annotation { "Feature Type Name" : "Feature", "Feature Type Description" : "" }
export const myFeature = defineFeature(function(context is Context, id is Id, definition is map)
    precondition{}
    {
        {
            var Q0;
            Q0=qCreatedBy(makeId("Top.planeOp"),FACE);
            var sketch = newSketch(context, id + "F0", { "sketchPlane" : qUnion([Q0])});
            skLineSegment(sketch, "E0.bottom", {"start": v(50.8, -25.4) * mm, "end": v(-50.8, -25.4) * mm});
            skLineSegment(sketch, "E0.top", {"start": v(50.8, 25.4) * mm, "end": v(-50.8, 25.4) * mm});
            skLineSegment(sketch, "E0.left", {"start": v(50.8, -25.4) * mm, "end": v(50.8, 25.4) * mm});
            skLineSegment(sketch, "E0.right", {"start": v(-50.8, -25.4) * mm, "end": v(-50.8, 25.4) * mm});
            skPoint(sketch, "E0.middle", {"position": v(0, 0) * mm});
            skSolve(sketch);
        }
        {
            var Q0;
            Q0 = qSketchRegion(id + "F0", true);
            extrude(context, id + "F1", {"entities" : qUnion([Q0]), "depth" : 6.35 * mm, "offsetDistance" : 25.4 * mm});
        }
        {
            var Q0;
            Q0=makeQuery(id+"F1.opExtrude","CAP_FACE",FACE,{"disambiguationData":[OSD([sQuery(id+"F0.wireOp",EDGE,"E0.bottom"),sQuery(id+"F0.wireOp",EDGE,"E0.top"),sQuery(id+"F0.wireOp",EDGE,"E0.left"),sQuery(id+"F0.wireOp",EDGE,"E0.right")])],"isStart":false});
            var sketch = newSketch(context, id + "F2", { "sketchPlane" : qUnion([Q0])});
            skText(sketch, "E1", { "text": "Jason Komisar\n", "fontName": "Tinos-Regular.ttf"});
            const initialGuessF2  = {"E1": [-0.04357, 0.00958, 1, 0, 0.01042]};
            skSetInitialGuess(sketch, initialGuessF2);
            skSolve(sketch);
        }
        {
            var Q0;
            Q0=makeQuery(id+"F2.imprint","IMPRINT",FACE,{"disambiguationData":[TD([[makeQuery(id+"F2.imprint","IMPRINT",EDGE,{"derivedFrom":sQuery(id+"F2.wireOp",EDGE,"E1.sketch_text.stroke-0")}),1.0]])]});
            var sketch = newSketch(context, id + "F3", { "sketchPlane" : qUnion([Q0])});
            skSolve(sketch);
        }
        {
            var Q0;
            Q0 = qSketchRegion(id + "F2", true);
            extrude(context, id + "F4", {"entities" : qUnion([Q0]), "operationType" : NewBodyOperationType.REMOVE, "oppositeDirection" : true, "depth" : 3.17 * mm, "offsetDistance" : 25.4 * mm});
        }
        {
            var Q0;
            Q0=makeQuery(id+"F3.imprint","IMPRINT",FACE,{"disambiguationData":[TD([[makeQuery(id+"F3.imprint","IMPRINT",EDGE,{"derivedFrom":makeQuery(id+"F2.imprint","IMPRINT",EDGE,{"derivedFrom":sQuery(id+"F2.wireOp",EDGE,"E1.sketch_text.stroke-0")})}),1.0]])]});
            var sketch = newSketch(context, id + "F5", { "sketchPlane" : qUnion([Q0])});
            skSolve(sketch);
        }
        {
            var Q0;
            Q0=makeQuery(id+"F3.imprint","IMPRINT",FACE,{"disambiguationData":[TD([[makeQuery(id+"F3.imprint","IMPRINT",EDGE,{"derivedFrom":makeQuery(id+"F2.imprint","IMPRINT",EDGE,{"derivedFrom":sQuery(id+"F2.wireOp",EDGE,"E1.sketch_text.stroke-0")})}),1.0]])]});
            var sketch = newSketch(context, id + "F6", { "sketchPlane" : qUnion([Q0])});
            skCircle(sketch, "E2", {"center": v(-31.63, -11.33) * mm, "radius": 9.27 * mm});
            skSolve(sketch);
        }
        {
            var Q0;
            Q0 = qSketchRegion(id + "F6", true);
            extrude(context, id + "F7", {"entities" : qUnion([Q0]), "operationType" : NewBodyOperationType.ADD, "depth" : 3.17 * mm, "offsetDistance" : 25.4 * mm});
        }
        {
            var Q0;
            Q0=makeQuery(id+"F7.opExtrude","CAP_FACE",FACE,{"disambiguationData":[OSD([sQuery(id+"F6.wireOp",EDGE,"E2")])],"isStart":false});
            var sketch = newSketch(context, id + "F8", { "sketchPlane" : qUnion([Q0])});
            skFitSpline(sketch, "E3", {"points": [v(-30.79, -3.96) * mm, v(-32.98, -4.5) * mm, v(-34.87, -5.85) * mm, v(-34.49, -9.56) * mm, v(-33.58, -11.22) * mm, v(-35.55, -14.77) * mm, v(-36.45, -17.26) * mm, v(-32.37, -19.08) * mm, v(-28.9, -19.15) * mm, v(-26.33, -17.64) * mm, v(-29.58, -13.18) * mm, v(-28.82, -11.97) * mm, v(-27.91, -11.37) * mm, v(-28.37, -10.39) * mm, v(-27.46, -9.4) * mm, v(-28.44, -6.16) * mm, v(-28.14, -4.95) * mm, v(-30.79, -3.96) * mm]});
            skSolve(sketch);
        }
        {
            var Q0;
            Q0=makeQuery(id+"F8.imprint","IMPRINT",FACE,{"disambiguationData":[TD([[makeQuery(id+"F8.imprint","IMPRINT",EDGE,{"derivedFrom":sQuery(id+"F8.wireOp",EDGE,"E3")}),1.0]])]});
            extrude(context, id + "F9", {"entities" : qUnion([Q0]), "operationType" : NewBodyOperationType.REMOVE, "oppositeDirection" : true, "depth" : 1.27 * mm, "offsetDistance" : 25.4 * mm});
        }
        {
            var Q0;
            Q0=makeQuery(id+"F6.imprint","IMPRINT",FACE,{"disambiguationData":[TD([[makeQuery(id+"F6.imprint","IMPRINT",EDGE,{"derivedFrom":sQuery(id+"F6.wireOp",EDGE,"E2")}),-1.0]])]});
            var sketch = newSketch(context, id + "F10", { "sketchPlane" : qUnion([Q0])});
            skFitSpline(sketch, "E4", {"points": [v(-4.38, -10.98) * mm, v(-4.11, -11.04) * mm, v(-2.78, -9.92) * mm, v(-1.4, -9.72) * mm, v(-1.46, -12.5) * mm, v(-1.79, -13.7) * mm, v(-2.45, -15.56) * mm, v(-3.25, -16.88) * mm, v(-3.05, -17.68) * mm, v(-2.05, -17.55) * mm, v(-1.46, -16.62) * mm, v(-1.06, -15.5) * mm, v(-0.73, -14.16) * mm, v(-0.8, -12.57) * mm, v(-0.66, -10.65) * mm, v(-0.66, -9.85) * mm, v(2.2, -9.78) * mm, v(2, -11.77) * mm, v(2.13, -12.57) * mm, v(1.8, -14.03) * mm, v(1.8, -15.3) * mm, v(2.2, -16.88) * mm, v(3.19, -17.81) * mm, v(4.65, -17.61) * mm, v(5.44, -16.68) * mm, v(5.64, -15.76) * mm, v(5.64, -15.16) * mm, v(5.38, -15.1) * mm, v(5.11, -15.76) * mm, v(4.38, -16.15) * mm, v(3.45, -15.89) * mm, v(2.79, -14.36) * mm, v(2.99, -13.1) * mm, v(3.05, -11.64) * mm, v(3.05, -10.65) * mm, v(3.39, -9.85) * mm, v(5.9, -9.59) * mm, v(5.97, -8.26) * mm, v(-2.65, -8.32) * mm, v(-3.65, -9.59) * mm, v(-4.38, -10.98) * mm]});
            skSolve(sketch);
        }
        {
            var Q0;
            Q0 = qSketchRegion(id + "F10", true);
            extrude(context, id + "F11", {"entities" : qUnion([Q0]), "operationType" : NewBodyOperationType.ADD, "depth" : 3.17 * mm, "offsetDistance" : 25.4 * mm});
        }
        {
            var Q0;
            Q0=makeQuery(id+"F5.imprint","IMPRINT",FACE,{"disambiguationData":[TD([[makeQuery(id+"F5.imprint","IMPRINT",EDGE,{"derivedFrom":makeQuery(id+"F3.imprint","IMPRINT",EDGE,{"derivedFrom":makeQuery(id+"F2.imprint","IMPRINT",EDGE,{"derivedFrom":sQuery(id+"F2.wireOp",EDGE,"E1.sketch_text.stroke-0")})})}),1.0]])]});
            var sketch = newSketch(context, id + "F12", { "sketchPlane" : qUnion([Q0])});
            skFitSpline(sketch, "E5", {"points": [v(20.54, -17.9) * mm, v(20.98, -16.12) * mm, v(21.4, -15.02) * mm, v(22.04, -13.4) * mm, v(23.03, -11.43) * mm, v(23.5, -10.36) * mm, v(23.62, -9.54) * mm, v(23.58, -8.04) * mm, v(23.62, -6.3) * mm, v(23.97, -4.84) * mm, v(24.53, -3.42) * mm, v(24.84, -2.67) * mm, v(25.47, -2.04) * mm, v(25.99, -1.45) * mm, v(29.81, -1.37) * mm, v(36.48, -1.4) * mm, v(37.15, -2.71) * mm, v(37.94, -4.96) * mm, v(39, -6.26) * mm, v(39.72, -7.96) * mm, v(40.54, -10.2) * mm, v(41.25, -12.81) * mm, v(41.85, -15.22) * mm, v(39.48, -17.5) * mm, v(36.52, -18.65) * mm, v(36.09, -18.69) * mm, v(35.7, -19.28) * mm, v(34.7, -19.32) * mm, v(32.61, -19.28) * mm, v(29.1, -19.28) * mm, v(23.58, -19.28) * mm, v(21.76, -19) * mm, v(20.54, -17.9) * mm]});
            skFitSpline(sketch, "E6", {"points": [v(34.03, -7.35) * mm, v(31.37, -7.22) * mm, v(29.45, -8.28) * mm, v(29.31, -8.61) * mm, v(31.24, -9.67) * mm, v(33.36, -9.47) * mm, v(34.22, -9.67) * mm, v(34.42, -10.36) * mm, v(33.63, -10.36) * mm, v(32.57, -10.36) * mm, v(31.64, -10.36) * mm, v(31.04, -10.87) * mm, v(31.64, -13.06) * mm, v(32.37, -12.26) * mm, v(34.69, -11.53) * mm, v(35.15, -9.74) * mm, v(34.36, -8.48) * mm, v(34.03, -7.35) * mm]});
            skFitSpline(sketch, "E7", {"points": [v(35.82, -7.48) * mm, v(35.62, -8.94) * mm, v(37.54, -9.67) * mm, v(38.74, -8.88) * mm, v(38.34, -7.55) * mm, v(37.48, -7.02) * mm, v(35.82, -7.48) * mm]});
            skCircle(sketch, "E8", {"center": v(36.83, -8.48) * mm, "radius": 0.52 * mm});
            skCircle(sketch, "E9", {"center": v(31.94, -8.36) * mm, "radius": 0.5 * mm});
            skFitSpline(sketch, "E10", {"points": [v(35.83, -10.13) * mm, v(36.23, -10.17) * mm, v(36.45, -10.65) * mm, v(36.52, -11.04) * mm, v(38.36, -12.64) * mm, v(39.09, -10.8) * mm, v(38.5, -10.36) * mm, v(37, -10.36) * mm, v(36.27, -9.88) * mm, v(35.83, -10.13) * mm]});
            skFitSpline(sketch, "E11", {"points": [v(32.88, -14.3) * mm, v(32.72, -14.69) * mm, v(32.18, -14.41) * mm, v(32.32, -14.04) * mm, v(32.88, -13.76) * mm, v(33.96, -12.84) * mm, v(34.65, -11.75) * mm, v(36.3, -11.73) * mm, v(38.32, -13.9) * mm, v(38.06, -14.28) * mm, v(37.16, -13.39) * mm, v(37.08, -14.14) * mm, v(36.66, -14.14) * mm, v(36.27, -12.7) * mm, v(36.11, -12.68) * mm, v(36.19, -14) * mm, v(35.8, -14.06) * mm, v(35.28, -12.48) * mm, v(35.18, -13.96) * mm, v(34.9, -14.16) * mm, v(34.42, -12.84) * mm, v(34.42, -14.06) * mm, v(33.94, -14.31) * mm, v(33.76, -13.53) * mm, v(32.88, -14.3) * mm]});
            skFitSpline(sketch, "E12", {"points": [v(21.06, -16.97) * mm, v(23.87, -15.14) * mm, v(25.51, -14.95) * mm, v(26.64, -10.36) * mm, v(29.03, -6.65) * mm, v(29.64, -6.32) * mm, v(29.17, -4.96) * mm, v(33.54, -5.34) * mm, v(32.88, -2.52) * mm, v(32.32, -1.25) * mm, v(31.1, -1.32) * mm, v(32.88, -4.12) * mm, v(32.88, -4.59) * mm, v(29.81, -1.37) * mm, v(25.99, -1.45) * mm, v(23.5, -10.36) * mm, v(21.06, -16.97) * mm]});
            skFitSpline(sketch, "E13", {"points": [v(32.88, -15.66) * mm, v(35, -18.47) * mm, v(35.93, -17.49) * mm, v(39.73, -14.9) * mm, v(38.98, -13.4) * mm, v(38.98, -12.47) * mm, v(39.64, -11.44) * mm, v(38.97, -10.54) * mm, v(38.74, -8.4) * mm, v(38.74, -7.55) * mm, v(41.04, -15.33) * mm, v(36.09, -18.69) * mm, v(35.7, -19.28) * mm, v(34.7, -19.32) * mm, v(32.88, -19.28) * mm, v(29.1, -19.28) * mm, v(28.38, -19.28) * mm, v(29.1, -18.65) * mm, v(28.42, -17.9) * mm, v(28.66, -16.31) * mm, v(32.32, -15.22) * mm, v(33.87, -14.67) * mm, v(38.34, -14.72) * mm, v(36.09, -16.64) * mm, v(34.7, -17.4) * mm, v(34.7, -17.2) * mm, v(32.88, -15.66) * mm]});
            skFitSpline(sketch, "E14", {"points": [v(22.57, -17.05) * mm, v(21.76, -17.9) * mm, v(25.99, -18.69) * mm, v(26.64, -16.65) * mm, v(29.1, -15.22) * mm, v(30.86, -15.22) * mm, v(27.48, -14.3) * mm, v(26.64, -15.22) * mm, v(24.84, -16.25) * mm, v(22.57, -17.05) * mm]});
            skFitSpline(sketch, "E15", {"points": [v(33.96, -2.04) * mm, v(36.48, -2.67) * mm, v(37.16, -4.57) * mm, v(36.09, -5.17) * mm, v(35.7, -4.44) * mm, v(34.7, -5.5) * mm, v(33.96, -2.04) * mm]});
            skFitSpline(sketch, "E16", {"points": [v(31.37, -14.14) * mm, v(27.3, -11.44) * mm, v(27.2, -8.88) * mm, v(29.81, -11.44) * mm, v(29.81, -12) * mm, v(29.81, -13.06) * mm, v(31.37, -14.14) * mm]});
            skFitSpline(sketch, "E17", {"points": [v(36.09, -5.5) * mm, v(35.56, -5.5) * mm, v(35.43, -5.9) * mm, v(35.7, -6.48) * mm, v(35.7, -6.7) * mm, v(36.09, -6.53) * mm, v(36.09, -6.17) * mm, v(36.09, -5.5) * mm]});
            skFitSpline(sketch, "E18", {"points": [v(31.73, -5.34) * mm, v(34.08, -6.46) * mm, v(34.16, -5.75) * mm, v(31.73, -5.34) * mm]});
            skFitSpline(sketch, "E19", {"points": [v(34.7, -7.85) * mm, v(35.42, -7.92) * mm, v(35.51, -7.7) * mm, v(34.8, -7.66) * mm, v(34.7, -7.85) * mm]});
            skFitSpline(sketch, "E20", {"points": [v(34.5, -8.33) * mm, v(34.54, -8.52) * mm, v(35.32, -8.4) * mm, v(35.46, -8.26) * mm, v(34.5, -8.33) * mm]});
            skFitSpline(sketch, "E21", {"points": [v(35.38, -9) * mm, v(35.36, -8.84) * mm, v(34.87, -8.8) * mm, v(34.87, -8.95) * mm, v(35.05, -9.03) * mm, v(35.38, -9) * mm]});
            skFitSpline(sketch, "E22", {"points": [v(39.01, -14.48) * mm, v(38.82, -14.67) * mm, v(38.93, -14.99) * mm, v(38.82, -15.13) * mm, v(38.5, -14.65) * mm, v(38.64, -14.34) * mm, v(39.01, -14.48) * mm]});
            skFitSpline(sketch, "E23", {"points": [v(28.1, -8.14) * mm, v(27.86, -8.44) * mm, v(28.36, -8.84) * mm, v(29.12, -8.2) * mm, v(30.28, -7.24) * mm, v(31.61, -6.88) * mm, v(32.88, -6.68) * mm, v(34.13, -7.01) * mm, v(34.63, -7.28) * mm, v(36.19, -6.91) * mm, v(37.71, -6.51) * mm, v(38.7, -7.48) * mm, v(38.21, -6.55) * mm, v(37.25, -6.18) * mm, v(36.39, -6.55) * mm, v(34.96, -7.04) * mm, v(32.04, -6.05) * mm, v(30.18, -6.46) * mm, v(29.45, -6.98) * mm, v(28.36, -7.7) * mm, v(28.1, -8.14) * mm]});
            skSolve(sketch);
        }
        {
            var Q0;
            Q0 = qSketchRegion(id + "F12", true);
            extrude(context, id + "F13", {"entities" : qUnion([Q0]), "operationType" : NewBodyOperationType.ADD, "depth" : 3.17 * mm, "offsetDistance" : 25.4 * mm});
        }
    });